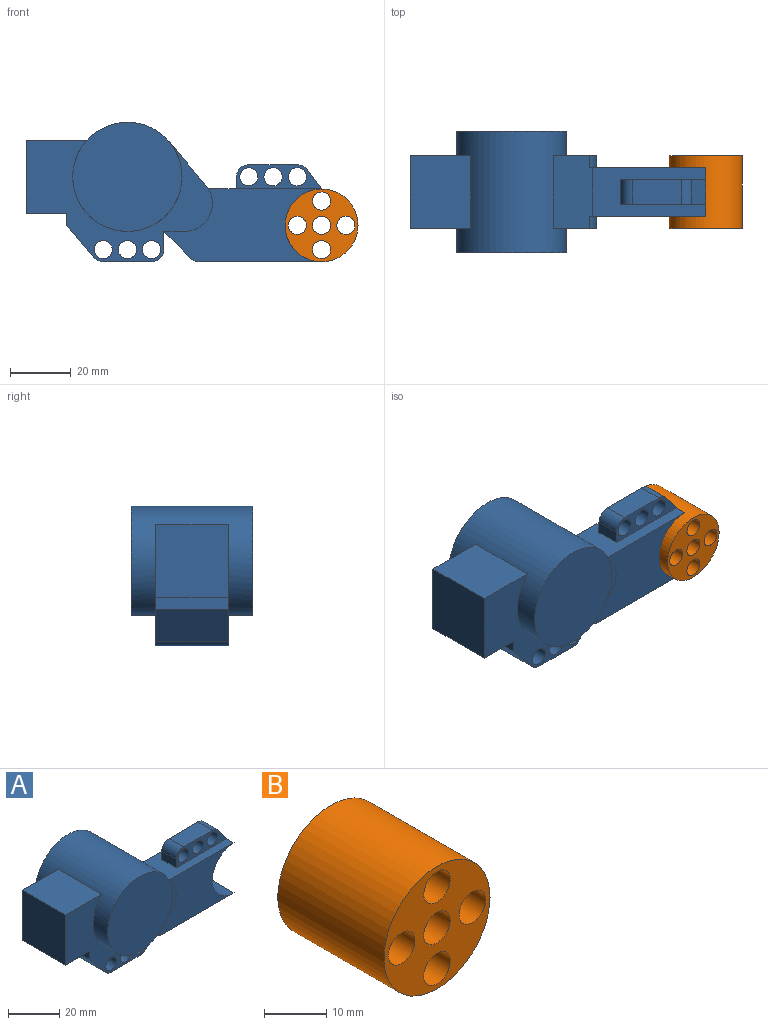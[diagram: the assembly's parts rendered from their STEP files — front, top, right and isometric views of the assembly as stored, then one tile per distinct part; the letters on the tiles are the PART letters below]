
ASSEMBLY  parts=2 mates=1
PART A: 39 faces, bbox 97.4x40x46 mm
  f0: plane 8x6.4mm, normal (0.8,0,0.6), area 64mm2, adj f1,f8,f9,f14
  f1: cylinder r=4mm len=8mm, axis (0,1,0), area 29.7mm2, adj f0,f2,f8,f9
  f2: plane 16x8mm, normal (0,0,1), area 128mm2, adj f1,f3,f8,f9
  f3: cylinder r=4mm len=8mm, axis (0,1,0), area 50.3mm2, adj f2,f7,f8,f9
  f4: cylinder r=3mm len=8mm, axis (0,1,0), area 150.8mm2, adj f8,f9
  f5: cylinder r=3mm len=8mm, axis (0,1,0), area 150.8mm2, adj f8,f9
  f6: cylinder r=3mm len=8mm, axis (0,1,0), area 150.8mm2, adj f8,f9
  f7: plane 8x4mm, normal (-1,0,0), area 32mm2, adj f3,f8,f9,f15
  f8: plane 28x8mm, normal (0,-1,0), area 111.2mm2, adj f0,f1,f2,f3,f4,f5,f6,f7
  f9: plane 28x8mm, normal (0,1,0), area 111.2mm2, adj f0,f1,f2,f3,f4,f5,f6,f7
  f10: plane 24x15.57mm, normal (0.77,0,0.64), area 475.1mm2, adj f15,f16,f17,f19,f32,f34,f35,f36
  f11: plane 16x8.83mm, normal (-0.71,0,-0.71), area 199.8mm2, adj f12,f16,f17,f28
  f12: cylinder r=4mm len=16mm, axis (0,1,0), area 50.3mm2, adj f11,f13,f16,f17
  f13: plane 40.34x16mm, normal (0,0,-1), area 645.5mm2, adj f12,f14,f16,f17
  f14: cylinder r=12mm len=24mm, axis (0,1,0), area 603.2mm2, adj f0,f13,f15,f16,f17
  f15: plane 37.15x16mm, normal (0,0,1), area 370.3mm2, adj f7,f8,f9,f10,f14,f16,f17
  f16: plane 52x25.22mm, normal (0,-1,0), area 767.9mm2, adj f10,f11,f12,f13,f14,f15,f18,f19
  f17: plane 52x25.22mm, normal (0,1,0), area 767.9mm2, adj f10,f11,f12,f13,f14,f15,f29,f32
  f18: plane 6.74x4mm, normal (0,0,-1), area 26.9mm2, adj f16,f19,f28,f34
  f19: cylinder r=9.26mm len=15.22mm, axis (0,1,0), area 84.1mm2, adj f10,f16,f18,f34
  f20: plane 24x20mm, normal (0,0,1), area 480mm2, adj f21,f34,f35,f36
  f21: plane 24x24mm, normal (-1,0,0), area 576mm2, adj f20,f22,f34,f35
  f22: plane 24x13.42mm, normal (0,0,-1), area 322mm2, adj f21,f23,f34,f35
  f23: plane 24x4mm, normal (-1,0,0), area 96mm2, adj f22,f24,f34,f35
  f24: plane 24x10.58mm, normal (-0.76,0,-0.65), area 332.6mm2, adj f23,f25,f34,f35
  f25: cylinder r=4mm len=24mm, axis (0,1,0), area 83.4mm2, adj f24,f26,f34,f35
  f26: plane 24x16mm, normal (0,0,-1), area 384mm2, adj f25,f27,f34,f35
  f27: cylinder r=4mm len=24mm, axis (0,1,0), area 150.8mm2, adj f26,f28,f34,f35
  f28: plane 24x6mm, normal (1,0,0), area 144mm2, adj f11,f18,f27,f29,f34,f35
  f29: plane 6.74x4mm, normal (0,0,-1), area 26.9mm2, adj f17,f28,f32,f35
  f30: cylinder r=3mm len=24mm, axis (0,1,0), area 452.4mm2, adj f34,f35
  f31: cylinder r=3mm len=24mm, axis (0,1,0), area 452.4mm2, adj f34,f35
  f32: cylinder r=9.26mm len=15.22mm, axis (0,1,0), area 84.1mm2, adj f10,f17,f29,f35
  f33: cylinder r=3mm len=24mm, axis (0,1,0), area 452.4mm2, adj f34,f35
  f34: plane 61.42x40mm, normal (0,-1,0), area 879.8mm2, adj f10,f18,f19,f20,f21,f22,f23,f24
  f35: plane 61.42x40mm, normal (0,1,0), area 879.8mm2, adj f10,f20,f21,f22,f23,f24,f25,f26
  f36: cylinder r=18mm len=40mm, axis (0,1,0), area 2549.9mm2, adj f10,f20,f34,f35,f37,f38
  f37: plane 36x36mm, normal (0,-1,0), area 1017.9mm2, adj f36
  f38: plane 36x36mm, normal (0,1,0), area 1017.9mm2, adj f36
PART B: 8 faces, bbox 24x24x24 mm
  f0: cylinder r=3mm len=24mm, axis (0,1,0), area 452.4mm2, adj f6,f7
  f1: cylinder r=3mm len=24mm, axis (0,1,0), area 452.4mm2, adj f6,f7
  f2: cylinder r=3mm len=24mm, axis (0,1,0), area 452.4mm2, adj f6,f7
  f3: cylinder r=3mm len=24mm, axis (0,1,0), area 452.4mm2, adj f6,f7
  f4: cylinder r=3mm len=24mm, axis (0,1,0), area 452.4mm2, adj f6,f7
  f5: cylinder r=12mm len=24mm, axis (0,1,0), area 1809.6mm2, adj f6,f7
  f6: plane 24x24mm, normal (0,-1,0), area 311mm2, adj f0,f1,f2,f3,f4,f5
  f7: plane 24x24mm, normal (0,1,0), area 311mm2, adj f0,f1,f2,f3,f4,f5
PLACE A at identity
PLACE B at identity
MATE revolute B.f0 <-> A.f14  axis (0,-1,0) through (0,0,0)mm
